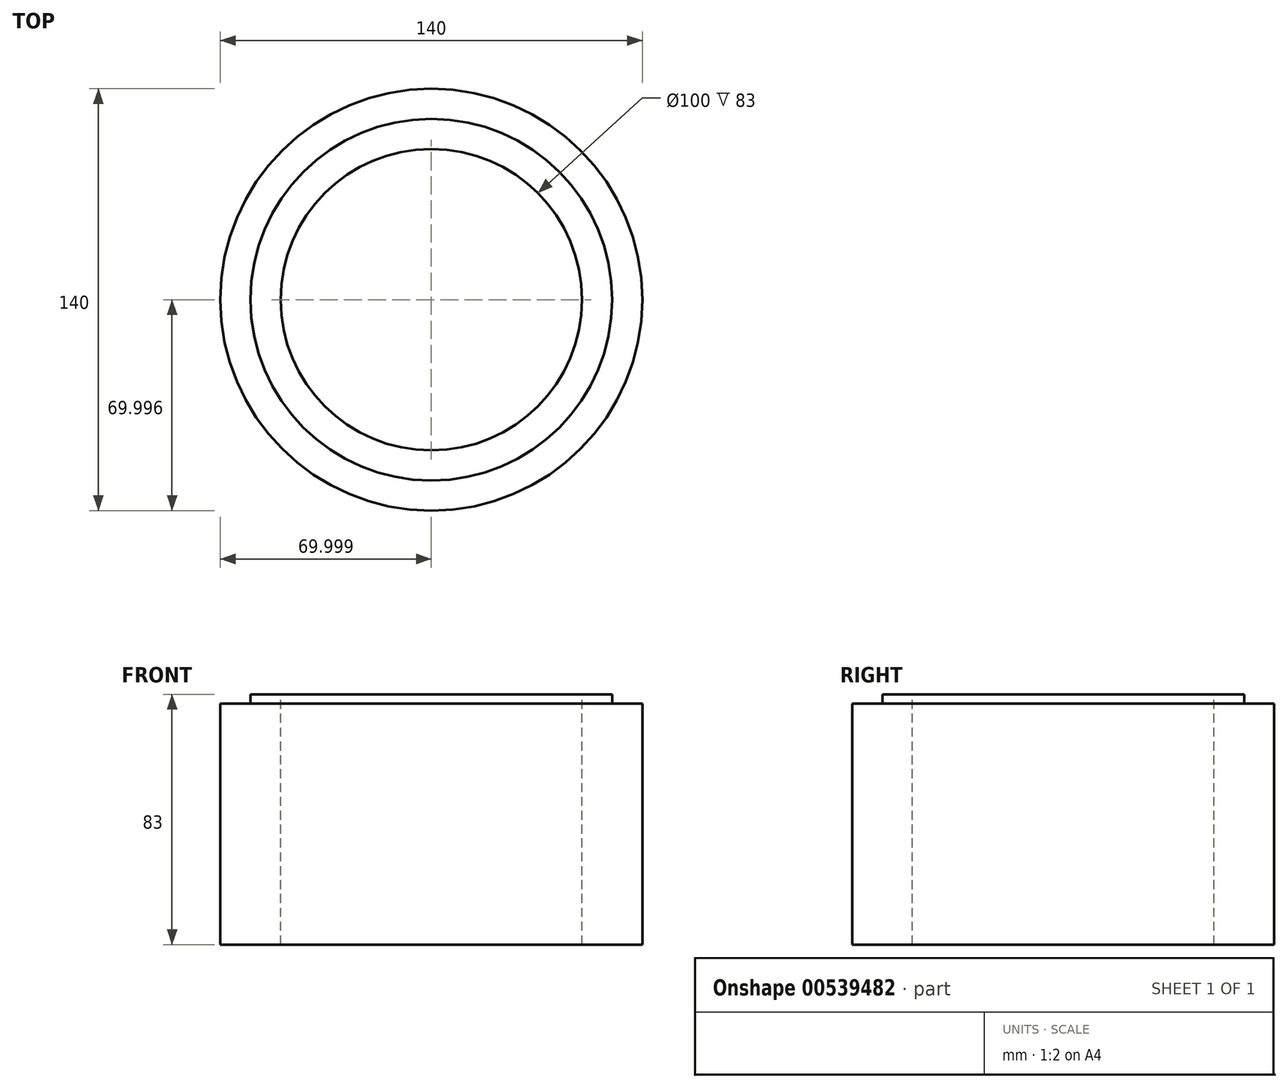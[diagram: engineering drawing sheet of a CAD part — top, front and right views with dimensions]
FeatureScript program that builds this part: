
annotation { "Feature Type Name" : "Feature", "Feature Type Description" : "" }
export const myFeature = defineFeature(function(context is Context, id is Id, definition is map)
    precondition{}
    {
        {
            var Q0;
            Q0=qCreatedBy(makeId("Top.planeOp"),FACE);
            var sketch = newSketch(context, id + "F0", { "sketchPlane" : qUnion([Q0])});
            skCircle(sketch, "E0", {"center": v(-43.9, -16.6) * mm, "radius": 70 * mm});
            skSolve(sketch);
        }
        {
            var Q0;
            Q0=makeQuery(id+"F0.imprint","IMPRINT",FACE,{"disambiguationData":[TD([[makeQuery(id+"F0.imprint","IMPRINT",EDGE,{"derivedFrom":sQuery(id+"F0.wireOp",EDGE,"E0")}),1.0]])]});
            extrude(context, id + "F1", {"entities" : qUnion([Q0]), "depth" : 80 * mm, "offsetDistance" : 25 * mm});
        }
        {
            var Q0;
            Q0=makeQuery(id+"F1.opExtrude","CAP_FACE",FACE,{"disambiguationData":[OSD([sQuery(id+"F0.wireOp",EDGE,"E0")])],"isStart":false});
            var sketch = newSketch(context, id + "F2", { "sketchPlane" : qUnion([Q0])});
            skCircle(sketch, "E1", {"center": v(-43.9, -16.6) * mm, "radius": 50 * mm});
            skSolve(sketch);
        }
        {
            var Q0;
            Q0=makeQuery(id+"F2.imprint","IMPRINT",FACE,{"disambiguationData":[TD([[makeQuery(id+"F2.imprint","IMPRINT",EDGE,{"derivedFrom":sQuery(id+"F2.wireOp",EDGE,"E1")}),1.0]])]});
            extrude(context, id + "F3", {"entities" : qUnion([Q0]), "operationType" : NewBodyOperationType.REMOVE, "oppositeDirection" : true, "depth" : 100 * mm, "offsetDistance" : 25 * mm});
        }
        {
            var Q0;
            Q0=makeQuery(id+"F1.opExtrude","CAP_FACE",FACE,{"disambiguationData":[OSD([sQuery(id+"F0.wireOp",EDGE,"E0")])],"isStart":false});
            var sketch = newSketch(context, id + "F4", { "sketchPlane" : qUnion([Q0])});
            skCircle(sketch, "E2", {"center": v(-43.9, -16.6) * mm, "radius": 50 * mm});
            skCircle(sketch, "E3", {"center": v(-43.9, -16.6) * mm, "radius": 60 * mm});
            skSolve(sketch);
        }
        {
            var Q0;
            Q0=makeQuery(id+"F4.imprint","IMPRINT",FACE,{"disambiguationData":[TD([[makeQuery(id+"F4.imprint","IMPRINT",EDGE,{"derivedFrom":sQuery(id+"F4.wireOp",EDGE,"E2")}),-1.0]])]});
            extrude(context, id + "F5", {"entities" : qUnion([Q0]), "operationType" : NewBodyOperationType.ADD, "depth" : 3 * mm, "offsetDistance" : 25 * mm});
        }
    });
